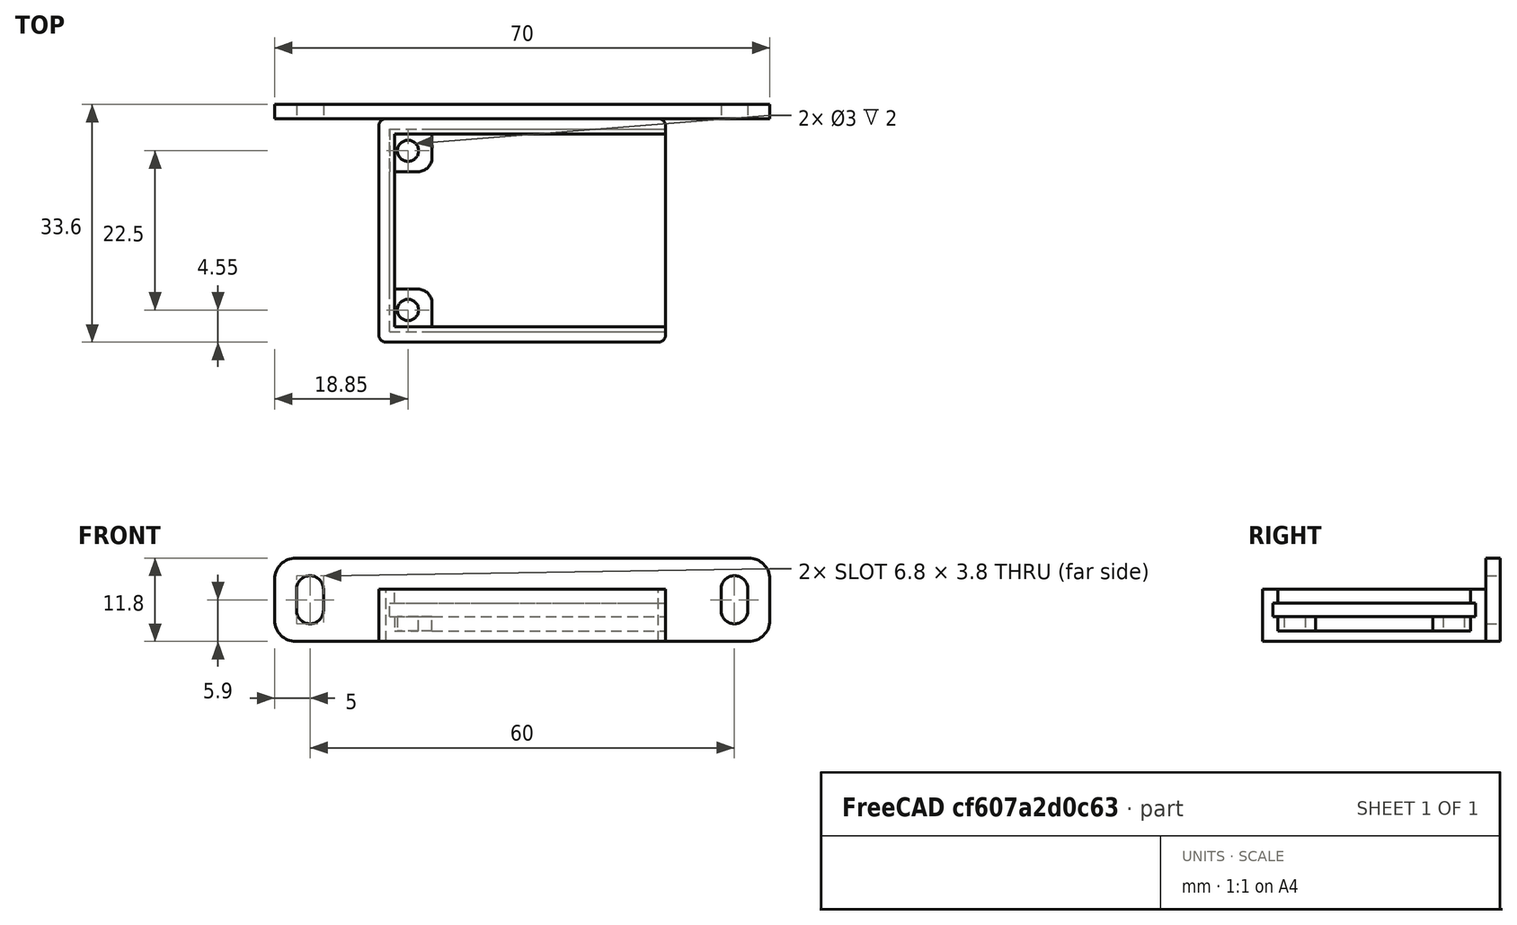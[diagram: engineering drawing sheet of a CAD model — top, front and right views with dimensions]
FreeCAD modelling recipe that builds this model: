
FCSTD DOCUMENT  (FreeCAD 0.20R29410 (Git))
Label: led_array_8x7
License: FreeArt
LicenseURL: http://artlibre.org/licence/lal
objects: Part::Box×4, Part::MultiFuse×4, Part::Fillet×2, Part::Cut×2, Spreadsheet::Sheet×1, Part::Cylinder×1, Part::Mirroring×1, Part::Feature×1, App::Part×1
note: 15 computed .brp shape members not serialized (recipe doc carries the construction recipe); baked Part::Feature solids carry a one-line shape summary decoded from their .brp

FEATURE [Spreadsheet::Sheet] Spreadsheet  label="p"
  cells = A1=pcb_x; B1(pcb_x)=39; A2=pcb_y; B2(pcb_y)=28.6; A3=pcb_z; B3(pcb_z)=1.9; A4=pcb_under; B4(pcb_under)=2; A5=side_wall; B5(side_wall)=1.5; A6=pcb_side_lane; B6(pcb_side_lane)=0.7; A7=bottom_wall; B7(bottom_wall)=1.5; A8=pcb_above; B8(pcb_above)=2; A9=hole_dist_y; B9(hole_dist_y)=22.5; A10=hole_off_x; B10(hole_off_x)=2.6; A11=hole_r; B11(hole_r)=1.5; A12=hole_stand_x; B12(hole_stand_x)=6; A13=hole_stand_y; B13(hole_stand_y)=6
FEATURE [Part::Box] Box  label="external cube"
  AttacherType = Attacher::AttachEngine3D
  Height = 7.4
  Length = 40.5
  Width = 31.6
  expr: Height = <<p>>.bottom_wall + <<p>>.pcb_under + <<p>>.pcb_z + <<p>>.pcb_above
  expr: Length = <<p>>.pcb_x + <<p>>.side_wall
  expr: Width = <<p>>.pcb_y + 2 * <<p>>.side_wall
FEATURE [Part::Box] Box006  label="internal cube"
  AttacherType = Attacher::AttachEngine3D
  Height = 5.9
  Length = 39.1
  Placement = pos=(2.2,2.2,1.5) rot=(0,0,1;0rad)
  Width = 27.2
  expr: .Placement.Base.x = <<p>>.side_wall + <<p>>.pcb_side_lane
  expr: .Placement.Base.y = <<p>>.side_wall + <<p>>.pcb_side_lane
  expr: .Placement.Base.z = <<p>>.bottom_wall
  expr: Height = <<p>>.pcb_under + <<p>>.pcb_z + <<p>>.pcb_above
  expr: Length = <<p>>.pcb_x - 2 * <<p>>.pcb_side_lane + <<p>>.side_wall
  expr: Width = <<p>>.pcb_y - 2 * <<p>>.pcb_side_lane
FEATURE [Part::Box] Box007  label="pcb extract cube"
  AttacherType = Attacher::AttachEngine3D
  Height = 1.9
  Length = 39
  Placement = pos=(1.5,1.5,3.5) rot=(0,0,1;0rad)
  Width = 28.6
  expr: .Placement.Base.x = <<p>>.side_wall
  expr: .Placement.Base.y = <<p>>.side_wall
  expr: .Placement.Base.z = <<p>>.bottom_wall + <<p>>.pcb_under
  expr: Height = <<p>>.pcb_z
  expr: Length = <<p>>.pcb_x
  expr: Width = <<p>>.pcb_y
FEATURE [Part::MultiFuse] Fusion  label="extract fusion"
  Shapes = -> [Box006,Box007]
FEATURE [Part::Fillet] Fillet  label="external fillet"
  Base = -> Box
  Edges = 4 edges r=1: [Edge1,Edge3,Edge5,Edge7]
FEATURE [Part::Box] Box008  label="hole stand"
  AttacherType = Attacher::AttachEngine3D
  Height = 2
  Length = 6
  Placement = pos=(1.5,1.5,1.5) rot=(0,0,1;0rad)
  Width = 6
  expr: .Placement.Base.x = <<p>>.side_wall
  expr: .Placement.Base.y = <<p>>.side_wall
  expr: .Placement.Base.z = <<p>>.bottom_wall
  expr: Height = <<p>>.pcb_under
  expr: Length = <<p>>.hole_stand_x
  expr: Width = <<p>>.hole_stand_y
FEATURE [Part::Cylinder] Cylinder  label="hole"
  Angle = 360
  AttacherType = Attacher::AttachEngine3D
  FirstAngle = 0
  Height = 10
  Placement = pos=(4.1,4.55,0) rot=(0,0,1;0rad)
  Radius = 1.5
  SecondAngle = 0
  expr: .Placement.Base.x = <<p>>.hole_off_x + <<p>>.side_wall
  expr: .Placement.Base.y = <<p>>.side_wall + (<<p>>.pcb_y - <<p>>.hole_dist_y) / 2
  expr: Radius = <<p>>.hole_r
FEATURE [Part::Fillet] Fillet001  label="hole stand fillet"
  Base = -> Box008
  Edges = 1 edges r=2: [Edge7]
FEATURE [Part::Cut] Cut002003  label="hole cut"
  Base = -> Fillet001
  Tool = -> Cylinder
FEATURE [Part::Mirroring] Part__Mirroring  label="hole stand (Mirror #1)"
  Base = (0,15.8,0)
  Normal = (0,1,0)
  Source = -> Cut002003
  expr: .Base.y = <<p>>.pcb_y / 2 + <<p>>.side_wall
FEATURE [Part::MultiFuse] Fusion002  label="hole fusion"
  Shapes = -> [Cut002003,Part__Mirroring]
FEATURE [Part::Feature] Body002002  label="attach plane x reverse rotated dir002"
  Placement = pos=(-14.75,33.6,0) rot=(1,0,0;1.5708rad)
  shape: bbox 70 x 2 x 11.8 mm, 18 faces (baked)
FEATURE [Part::MultiFuse] Fusion001  label="solid fusion"
  Shapes = -> [Fillet,Body002002]
FEATURE [Part::Cut] Cut  label="sd card cut"
  Base = -> Fusion001
  Tool = -> Fusion
FEATURE [Part::MultiFuse] Fusion003  label="sd card fusion"
  Shapes = -> [Fusion002,Cut]
FEATURE [App::Part] Part  label="pcb part"
  Group = -> [Box,Fillet,Fusion001,Fusion,Box007,Box006,Cut,Part__Mirroring,Cut002003,Fusion002,Box008,Fillet001,Cylinder,Fusion003]
  Origin = -> Origin
